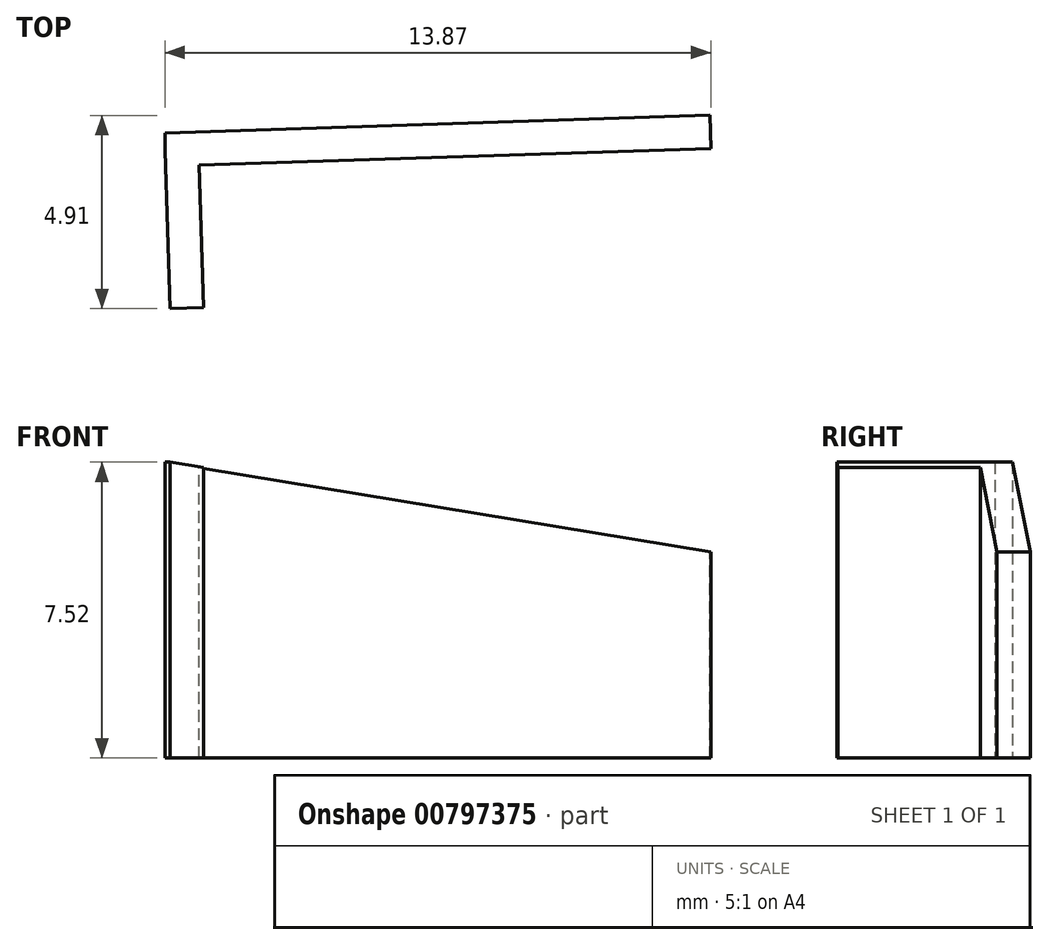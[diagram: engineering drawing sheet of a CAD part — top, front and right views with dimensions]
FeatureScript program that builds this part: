
annotation { "Feature Type Name" : "Feature", "Feature Type Description" : "" }
export const myFeature = defineFeature(function(context is Context, id is Id, definition is map)
    precondition{}
    {
        {
            var Q0;
            Q0=qCreatedBy(makeId("Top.planeOp"),FACE);
            var sketch = newSketch(context, id + "F0", { "sketchPlane" : qUnion([Q0])});
            skLineSegment(sketch, "E0", {"start": v(0, 0) * mm, "end": v(18.12, 0) * mm, "construction": true});
            skLineSegment(sketch, "E1", {"start": v(0, 0) * mm, "end": v(0, 21.64) * mm, "construction": true});
            skLineSegment(sketch, "E2", {"start": v(18.12, 0) * mm, "end": v(0, 21.64) * mm});
            skLineSegment(sketch, "E3", {"start": v(0, 21.64) * mm, "end": v(-9.26, 21.64) * mm, "construction": true});
            skLineSegment(sketch, "E4", {"start": v(-9.26, 21.64) * mm, "end": v(-9.26, 25.88) * mm, "construction": true});
            skArc(sketch, "E5", {"start": v(0, 21.64) * mm, "mid": v(-4.15, 24.81) * mm, "end": v(-9.26, 25.88) * mm});
            skLineSegment(sketch, "E6", {"start": v(-9.26, 25.88) * mm, "end": v(-23.1, 25.44) * mm});
            skLineSegment(sketch, "E7", {"start": v(-9.26, 25.88) * mm, "end": v(-12.6, 25.83) * mm, "construction": true});
            skLineSegment(sketch, "E8.0", {"start": v(-9.27, 26.28) * mm, "end": v(-23.12, 25.84) * mm});
            skArc(sketch, "E8.1", {"start": v(0.3, 21.9) * mm, "mid": v(-3.99, 25.17) * mm, "end": v(-9.27, 26.28) * mm});
            skLineSegment(sketch, "E8.2", {"start": v(18.43, 0.26) * mm, "end": v(0.3, 21.9) * mm});
            skLineSegment(sketch, "E9", {"start": v(-23.12, 25.84) * mm, "end": v(-23.1, 25.44) * mm});
            skLineSegment(sketch, "E10", {"start": v(18.12, 0) * mm, "end": v(18.43, 0.26) * mm});
            skLineSegment(sketch, "E11", {"start": v(-9.27, 26.28) * mm, "end": v(-9.28, 26.73) * mm});
            skLineSegment(sketch, "E12", {"start": v(-9.28, 26.73) * mm, "end": v(-23.13, 26.29) * mm});
            skLineSegment(sketch, "E13", {"start": v(-23.13, 26.29) * mm, "end": v(-23.12, 25.84) * mm});
            skSolve(sketch);
        }
        {
            var Q0;
            Q0=makeQuery(id+"F0.imprint","IMPRINT",FACE,{"disambiguationData":[TD([[makeQuery(id+"F0.imprint","IMPRINT",EDGE,{"derivedFrom":sQuery(id+"F0.wireOp",EDGE,"E2")}),-1.0]])]});
            var Q1;
            Q1=makeQuery(id+"F0.imprint","IMPRINT",FACE,{"disambiguationData":[TD([[makeQuery(id+"F0.imprint","IMPRINT",EDGE,{"derivedFrom":sQuery(id+"F0.wireOp",EDGE,"E8.0")}),-1.0]])]});
            extrude(context, id + "F1", {"entities" : qUnion([Q0, Q1]), "depth" : 11.4 * mm, "offsetDistance" : 25 * mm});
        }
        {
            var Q0;
            Q0=makeQuery(id+"F1.opExtrude","SWEPT_FACE",FACE,{"disambiguationData":[OSD([sQuery(id+"F0.wireOp",EDGE,"E2")])]});
            var sketch = newSketch(context, id + "F2", { "sketchPlane" : qUnion([Q0])});
            skLineSegment(sketch, "E14", {"start": v(11.64, 0) * mm, "end": v(11.64, 1.35) * mm});
            skLineSegment(sketch, "E15", {"start": v(-16.6, 0) * mm, "end": v(-16.6, 4.18) * mm});
            skLineSegment(sketch, "E16", {"start": v(-16.6, 4.18) * mm, "end": v(11.64, 1.35) * mm});
            skSolve(sketch);
        }
        {
            var Q0;
            Q0 = qSketchRegion(id + "F2", true);
            var Q1;
            {var subQ0=sQuery(id+"F2.wireOp",EDGE,"E16");Q1=makeQuery(id+"F2.imprint","IMPRINT",FACE,{"disambiguationData":[TD([[makeQuery(id+"F2.imprint","IMPRINT",EDGE,{"derivedFrom":subQ0}),1.0]])]});}
            extrude(context, id + "F3", {"entities" : qUnion([Q0, Q1]), "operationType" : NewBodyOperationType.REMOVE, "oppositeDirection" : true, "depth" : 25 * mm, "offsetDistance" : 25 * mm});
        }
        {
            var Q0;
            Q0=makeQuery(id+"F1.opExtrude","SWEPT_FACE",FACE,{"disambiguationData":[OSD([sQuery(id+"F0.wireOp",EDGE,"E6")])]});
            var sketch = newSketch(context, id + "F4", { "sketchPlane" : qUnion([Q0])});
            skLineSegment(sketch, "E17", {"start": v(-8.42, 0) * mm, "end": v(-8.42, 5.23) * mm});
            skLineSegment(sketch, "E18", {"start": v(-8.42, 0) * mm, "end": v(-21.42, 0) * mm});
            skLineSegment(sketch, "E19", {"start": v(-21.42, 0) * mm, "end": v(-21.42, 7.38) * mm});
            skLineSegment(sketch, "E20", {"start": v(-22.27, 7.52) * mm, "end": v(-8.42, 5.23) * mm});
            skLineSegment(sketch, "E21", {"start": v(-21.42, 0) * mm, "end": v(-32.62, 0) * mm});
            skLineSegment(sketch, "E22", {"start": v(-22.27, 0) * mm, "end": v(-32.62, 0) * mm});
            skLineSegment(sketch, "E23", {"start": v(-21.42, 7.38) * mm, "end": v(-21.42, 11.4) * mm});
            skLineSegment(sketch, "E24.0.0", {"start": v(-8.42, 0) * mm, "end": v(0.7, 0) * mm});
            skLineSegment(sketch, "E24.0.1", {"start": v(0.7, 0) * mm, "end": v(0.7, 4.18) * mm});
            skLineSegment(sketch, "E24.0.2", {"start": v(0.7, 4.18) * mm, "end": v(0.7, 11.4) * mm});
            skLineSegment(sketch, "E24.0.3", {"start": v(0.7, 11.4) * mm, "end": v(-8.42, 11.4) * mm});
            skLineSegment(sketch, "E24.0.4", {"start": v(-8.42, 11.4) * mm, "end": v(-8.42, 0) * mm});
            skLineSegment(sketch, "E25.0.0", {"start": v(18.11, 1.35) * mm, "end": v(0.7, 4.18) * mm});
            skLineSegment(sketch, "E25.0.1", {"start": v(0.7, 4.18) * mm, "end": v(0.7, 0) * mm});
            skLineSegment(sketch, "E25.0.2", {"start": v(0.7, 0) * mm, "end": v(18.11, 0) * mm});
            skLineSegment(sketch, "E25.0.3", {"start": v(18.11, 0) * mm, "end": v(18.11, 1.35) * mm});
            skLineSegment(sketch, "E26", {"start": v(-21.42, 11.4) * mm, "end": v(-8.42, 11.4) * mm});
            skLineSegment(sketch, "E27", {"start": v(-8.42, 5.23) * mm, "end": v(0.7, 4.18) * mm});
            skLineSegment(sketch, "E28", {"start": v(0.7, 11.4) * mm, "end": v(0.7, 4.18) * mm});
            skLineSegment(sketch, "E29", {"start": v(18.11, 1.35) * mm, "end": v(18.11, 8.57) * mm});
            skLineSegment(sketch, "E30", {"start": v(0.7, 11.4) * mm, "end": v(18.11, 11.4) * mm});
            skLineSegment(sketch, "E31", {"start": v(18.11, 8.57) * mm, "end": v(18.11, 11.4) * mm});
            skLineSegment(sketch, "E32", {"start": v(-21.42, 11.4) * mm, "end": v(-22.27, 11.4) * mm});
            skLineSegment(sketch, "E33", {"start": v(-22.27, 11.4) * mm, "end": v(-22.27, 7.52) * mm});
            skSolve(sketch);
        }
        {
            var Q0;
            {var subQ2=sQuery(id+"F4.wireOp",EDGE,"E23");var subQ4=makeQuery(id+"F4.imprint","IMPRINT",EDGE,{"derivedFrom":subQ2});Q0=qUnion([makeQuery(id+"F4.imprint","IMPRINT",FACE,{"disambiguationData":[TD([[subQ4,1.0]])]}),makeQuery(id+"F4.imprint","IMPRINT",FACE,{"disambiguationData":[TD([[subQ4,-1.0]])]})]);}
            var Q1;
            Q1=makeQuery(id+"F4.imprint","IMPRINT",FACE,{"disambiguationData":[TD([[makeQuery(id+"F4.imprint","IMPRINT",EDGE,{"derivedFrom":sQuery(id+"F4.wireOp",EDGE,"E24.0.2")}),1.0]])]});
            var Q2;
            Q2=makeQuery(id+"F4.imprint","IMPRINT",FACE,{"disambiguationData":[TD([[makeQuery(id+"F4.imprint","IMPRINT",EDGE,{"derivedFrom":sQuery(id+"F4.wireOp",EDGE,"E24.0.2")}),-1.0]])]});
            extrude(context, id + "F5", {"entities" : qUnion([Q0, Q1, Q2]), "operationType" : NewBodyOperationType.REMOVE, "endBound" : BoundingType.SYMMETRIC, "oppositeDirection" : true, "depth" : 25 * mm, "offsetDistance" : 25 * mm});
        }
        {
            var Q0;
            Q0=makeQuery(id+"F1.opExtrude","SWEPT_FACE",FACE,{"disambiguationData":[OSD([sQuery(id+"F0.wireOp",EDGE,"E6")])]});
            var sketch = newSketch(context, id + "F6", { "sketchPlane" : qUnion([Q0])});
            skLineSegment(sketch, "E34", {"start": v(-22.27, 0) * mm, "end": v(-21.42, 0) * mm});
            skLineSegment(sketch, "E35", {"start": v(-21.42, 0) * mm, "end": v(-21.42, 7.38) * mm});
            skLineSegment(sketch, "E36", {"start": v(-21.42, 7.38) * mm, "end": v(-22.27, 7.52) * mm});
            skSolve(sketch);
        }
        {
            var Q0;
            Q0=makeQuery(id+"F6.imprint","IMPRINT",FACE,{"disambiguationData":[TD([[makeQuery(id+"F6.imprint","IMPRINT",EDGE,{"derivedFrom":sQuery(id+"F6.wireOp",EDGE,"E34")}),-1.0]])]});
            extrude(context, id + "F7", {"entities" : qUnion([Q0]), "operationType" : NewBodyOperationType.ADD, "depth" : 3.62 * mm, "offsetDistance" : 25 * mm});
        }
        {
            var Q0;
            Q0=makeQuery(id+"F1.opExtrude","SWEPT_FACE",FACE,{"disambiguationData":[OSD([sQuery(id+"F0.wireOp",EDGE,"E6")])]});
            var sketch = newSketch(context, id + "F8", { "sketchPlane" : qUnion([Q0])});
            skLineSegment(sketch, "E37", {"start": v(-8.42, 0) * mm, "end": v(-8.42, 50) * mm});
            skLineSegment(sketch, "E38", {"start": v(-8.42, 50) * mm, "end": v(51.57, 51.02) * mm});
            skLineSegment(sketch, "E39", {"start": v(51.57, 51.02) * mm, "end": v(53.21, -45.26) * mm});
            skLineSegment(sketch, "E40", {"start": v(-8.42, 0) * mm, "end": v(-8.42, -8.6) * mm});
            skLineSegment(sketch, "E41", {"start": v(-8.42, -8.6) * mm, "end": v(53.21, -45.26) * mm});
            skSolve(sketch);
        }
        {
            var Q0;
            {var subQ0=sQuery(id+"F8.wireOp",EDGE,"E38");Q0=makeQuery(id+"F8.imprint","IMPRINT",FACE,{"disambiguationData":[TD([[makeQuery(id+"F8.imprint","IMPRINT",EDGE,{"derivedFrom":subQ0}),-1.0]])]});}
            extrude(context, id + "F9", {"entities" : qUnion([Q0]), "operationType" : NewBodyOperationType.REMOVE, "oppositeDirection" : true, "depth" : 25 * mm, "offsetDistance" : 25 * mm, "hasSecondDirection" : true, "secondDirectionOppositeDirection" : false, "secondDirectionDepth" : 49.7 * mm});
        }
    });
